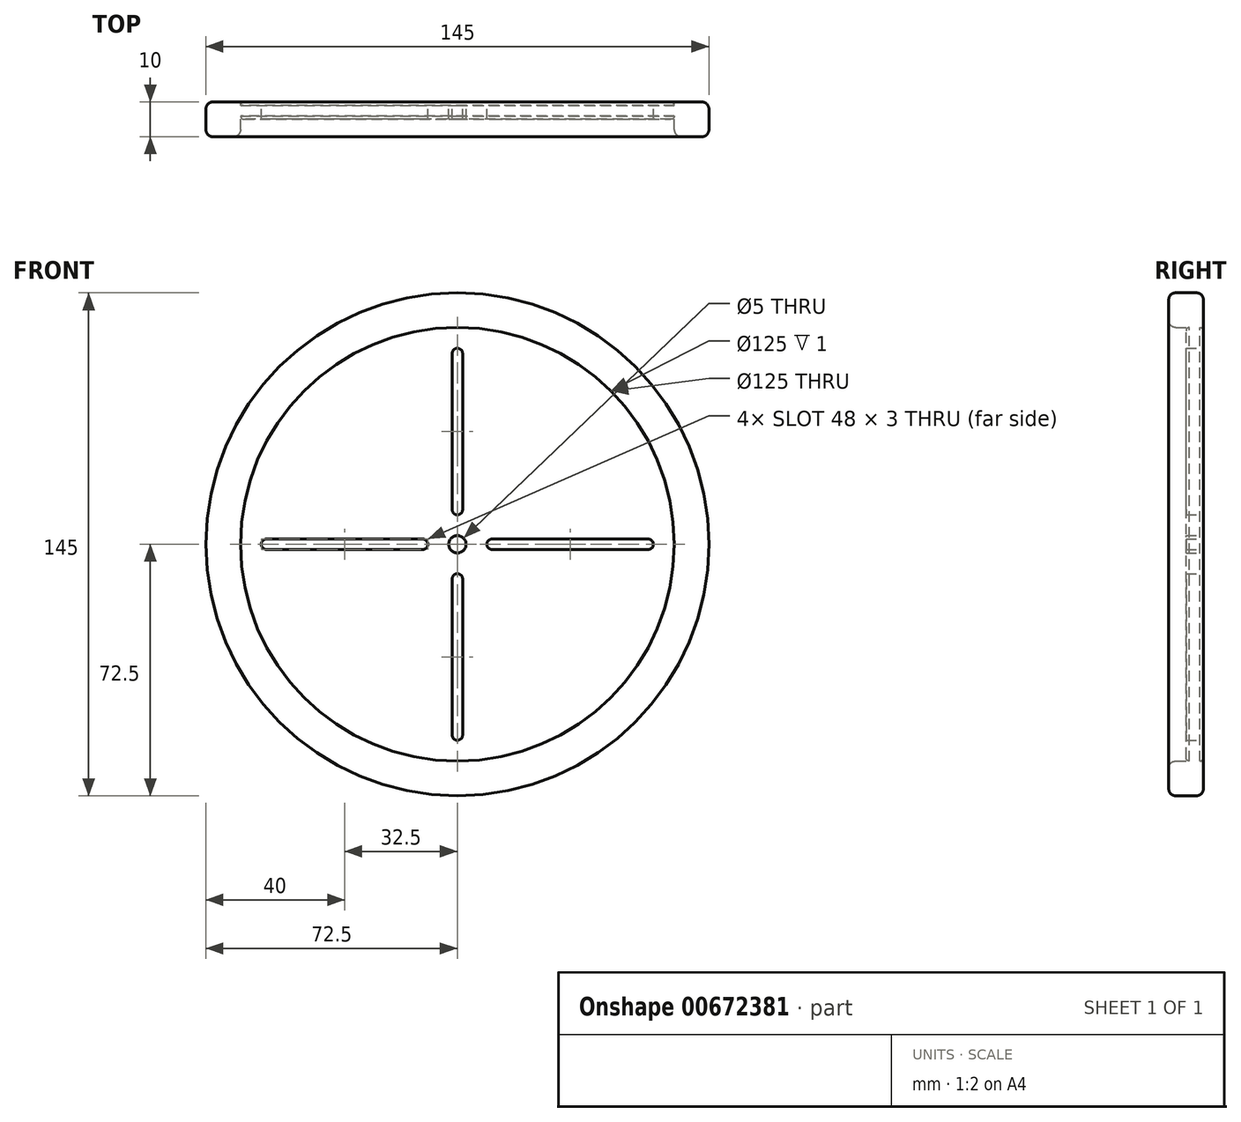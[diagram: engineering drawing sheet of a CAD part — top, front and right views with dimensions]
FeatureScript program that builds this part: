
annotation { "Feature Type Name" : "Feature", "Feature Type Description" : "" }
export const myFeature = defineFeature(function(context is Context, id is Id, definition is map)
    precondition{}
    {
        {
            var Q0;
            Q0=qCreatedBy(makeId("Front.planeOp"),FACE);
            var sketch = newSketch(context, id + "F0", { "sketchPlane" : qUnion([Q0])});
            skCircle(sketch, "E0", {"center": v(0, 0) * mm, "radius": 62.5 * mm});
            skLineSegment(sketch, "E1", {"start": v(0, 10) * mm, "end": v(0, 55) * mm});
            skArc(sketch, "E2.0.startCap", {"start": v(1.5, 10) * mm, "mid": v(0, 8.5) * mm, "end": v(-1.5, 10) * mm});
            skArc(sketch, "E2.0.endCap", {"start": v(-1.5, 55) * mm, "mid": v(0, 56.5) * mm, "end": v(1.5, 55) * mm});
            skLineSegment(sketch, "E2.0.left", {"start": v(-1.5, 10) * mm, "end": v(-1.5, 55) * mm});
            skLineSegment(sketch, "E2.0.right", {"start": v(1.5, 10) * mm, "end": v(1.5, 55) * mm});
            skArc(sketch, "E3.MirrorCS", {"start": v(1.5, -10) * mm, "mid": v(0, -8.5) * mm, "end": v(-1.5, -10) * mm});
            skLineSegment(sketch, "E4.MirrorCS", {"start": v(1.5, -10) * mm, "end": v(1.5, -55) * mm});
            skArc(sketch, "E5.MirrorCS", {"start": v(-1.5, -55) * mm, "mid": v(0, -56.5) * mm, "end": v(1.5, -55) * mm});
            skLineSegment(sketch, "E6.MirrorCS", {"start": v(-1.5, -10) * mm, "end": v(-1.5, -55) * mm});
            skLineSegment(sketch, "E7", {"start": v(10, 0) * mm, "end": v(55, 0) * mm});
            skArc(sketch, "E8.0.startCap", {"start": v(10, -1.5) * mm, "mid": v(8.5, 0) * mm, "end": v(10, 1.5) * mm});
            skArc(sketch, "E8.0.endCap", {"start": v(55, 1.5) * mm, "mid": v(56.5, 0) * mm, "end": v(55, -1.5) * mm});
            skLineSegment(sketch, "E8.0.left", {"start": v(10, 1.5) * mm, "end": v(55, 1.5) * mm});
            skLineSegment(sketch, "E8.0.right", {"start": v(10, -1.5) * mm, "end": v(55, -1.5) * mm});
            skArc(sketch, "E9.MirrorCS", {"start": v(-10, -1.5) * mm, "mid": v(-8.5, 0) * mm, "end": v(-10, 1.5) * mm});
            skLineSegment(sketch, "E10.MirrorCS", {"start": v(-10, -1.5) * mm, "end": v(-55, -1.5) * mm});
            skArc(sketch, "E11.MirrorCS", {"start": v(-55, 1.5) * mm, "mid": v(-56.5, 0) * mm, "end": v(-55, -1.5) * mm});
            skLineSegment(sketch, "E12.MirrorCS", {"start": v(-10, 1.5) * mm, "end": v(-55, 1.5) * mm});
            skCircle(sketch, "E13.0", {"center": v(0, 0) * mm, "radius": 72.5 * mm});
            skCircle(sketch, "E14", {"center": v(0, 0) * mm, "radius": 2.5 * mm});
            skSolve(sketch);
        }
        {
            var Q0;
            Q0=makeQuery(id+"F0.imprint","IMPRINT",FACE,{"disambiguationData":[TD([[makeQuery(id+"F0.imprint","IMPRINT",EDGE,{"derivedFrom":sQuery(id+"F0.wireOp",EDGE,"E0")}),1.0]])]});
            extrude(context, id + "F1", {"entities" : qUnion([Q0]), "depth" : 5 * mm, "offsetDistance" : 25 * mm});
        }
        {
            var Q0;
            Q0=makeQuery(id+"F1.opExtrude","CAP_EDGE",EDGE,{"disambiguationData":[OSD([sQuery(id+"F0.wireOp",EDGE,"E0")])],"isStart":false});
            var Q1;
            Q1=makeQuery(id+"F1.opExtrude","CAP_EDGE",EDGE,{"disambiguationData":[OSD([sQuery(id+"F0.wireOp",EDGE,"E0")])],"isStart":true});
            fillet(context, id + "F2", {"entities" : qUnion([Q0, Q1]), "radius" : 1 * mm, "tangentPropagation" : true, "allowEdgeOverflow" : false});
        }
        {
            var Q0;
            Q0=makeQuery(id+"F0.imprint","IMPRINT",FACE,{"disambiguationData":[TD([[makeQuery(id+"F0.imprint","IMPRINT",EDGE,{"derivedFrom":sQuery(id+"F0.wireOp",EDGE,"E0")}),-1.0]])]});
            extrude(context, id + "F3", {"entities" : qUnion([Q0]), "operationType" : NewBodyOperationType.ADD, "depth" : 10 * mm, "offsetDistance" : 25 * mm});
        }
        {
            var Q0;
            {var subQ0=sQuery(id+"F0.wireOp",EDGE,"E0");Q0=makeQuery(id+"F2.opFillet","BLEND_EDGE",EDGE,{"blendedFrom":[makeQuery(id+"F1.opExtrude","CAP_EDGE",EDGE,{"disambiguationData":[OSD([subQ0])],"isStart":false}),makeQuery(id+"F1.opExtrude","CAP_FACE",FACE,{"disambiguationData":[OSD([subQ0,sQuery(id+"F0.wireOp",EDGE,"E2.0.startCap"),sQuery(id+"F0.wireOp",EDGE,"E2.0.endCap"),sQuery(id+"F0.wireOp",EDGE,"E2.0.left"),sQuery(id+"F0.wireOp",EDGE,"E2.0.right"),sQuery(id+"F0.wireOp",EDGE,"E3.MirrorCS"),sQuery(id+"F0.wireOp",EDGE,"E4.MirrorCS"),sQuery(id+"F0.wireOp",EDGE,"E5.MirrorCS"),sQuery(id+"F0.wireOp",EDGE,"E6.MirrorCS"),sQuery(id+"F0.wireOp",EDGE,"E8.0.startCap"),sQuery(id+"F0.wireOp",EDGE,"E8.0.endCap"),sQuery(id+"F0.wireOp",EDGE,"E8.0.left"),sQuery(id+"F0.wireOp",EDGE,"E8.0.right"),sQuery(id+"F0.wireOp",EDGE,"E9.MirrorCS"),sQuery(id+"F0.wireOp",EDGE,"E10.MirrorCS"),sQuery(id+"F0.wireOp",EDGE,"E11.MirrorCS"),sQuery(id+"F0.wireOp",EDGE,"E12.MirrorCS")])],"isStart":false})],"blendedInto":[makeQuery(id+"F1.opExtrude","CAP_FACE",FACE,{"disambiguationData":[OSD([subQ0,sQuery(id+"F0.wireOp",EDGE,"E2.0.startCap"),sQuery(id+"F0.wireOp",EDGE,"E2.0.endCap"),sQuery(id+"F0.wireOp",EDGE,"E2.0.left"),sQuery(id+"F0.wireOp",EDGE,"E2.0.right"),sQuery(id+"F0.wireOp",EDGE,"E3.MirrorCS"),sQuery(id+"F0.wireOp",EDGE,"E4.MirrorCS"),sQuery(id+"F0.wireOp",EDGE,"E5.MirrorCS"),sQuery(id+"F0.wireOp",EDGE,"E6.MirrorCS"),sQuery(id+"F0.wireOp",EDGE,"E8.0.startCap"),sQuery(id+"F0.wireOp",EDGE,"E8.0.endCap"),sQuery(id+"F0.wireOp",EDGE,"E8.0.left"),sQuery(id+"F0.wireOp",EDGE,"E8.0.right"),sQuery(id+"F0.wireOp",EDGE,"E9.MirrorCS"),sQuery(id+"F0.wireOp",EDGE,"E10.MirrorCS"),sQuery(id+"F0.wireOp",EDGE,"E11.MirrorCS"),sQuery(id+"F0.wireOp",EDGE,"E12.MirrorCS")])],"isStart":false})]});}
            var Q1;
            Q1=makeQuery(id+"F3.opExtrude","CAP_EDGE",EDGE,{"disambiguationData":[OSD([sQuery(id+"F0.wireOp",EDGE,"E0")])],"isStart":false});
            var Q2;
            Q2=makeQuery(id+"F3.opExtrude","CAP_EDGE",EDGE,{"disambiguationData":[OSD([sQuery(id+"F0.wireOp",EDGE,"E13.0")])],"isStart":false});
            var Q3;
            Q3=makeQuery(id+"F3.opExtrude","CAP_EDGE",EDGE,{"disambiguationData":[OSD([sQuery(id+"F0.wireOp",EDGE,"E13.0")])],"isStart":true});
            fillet(context, id + "F4", {"entities" : qUnion([Q0, Q1, Q2, Q3]), "radius" : 2 * mm, "tangentPropagation" : true, "allowEdgeOverflow" : false});
        }
    });
